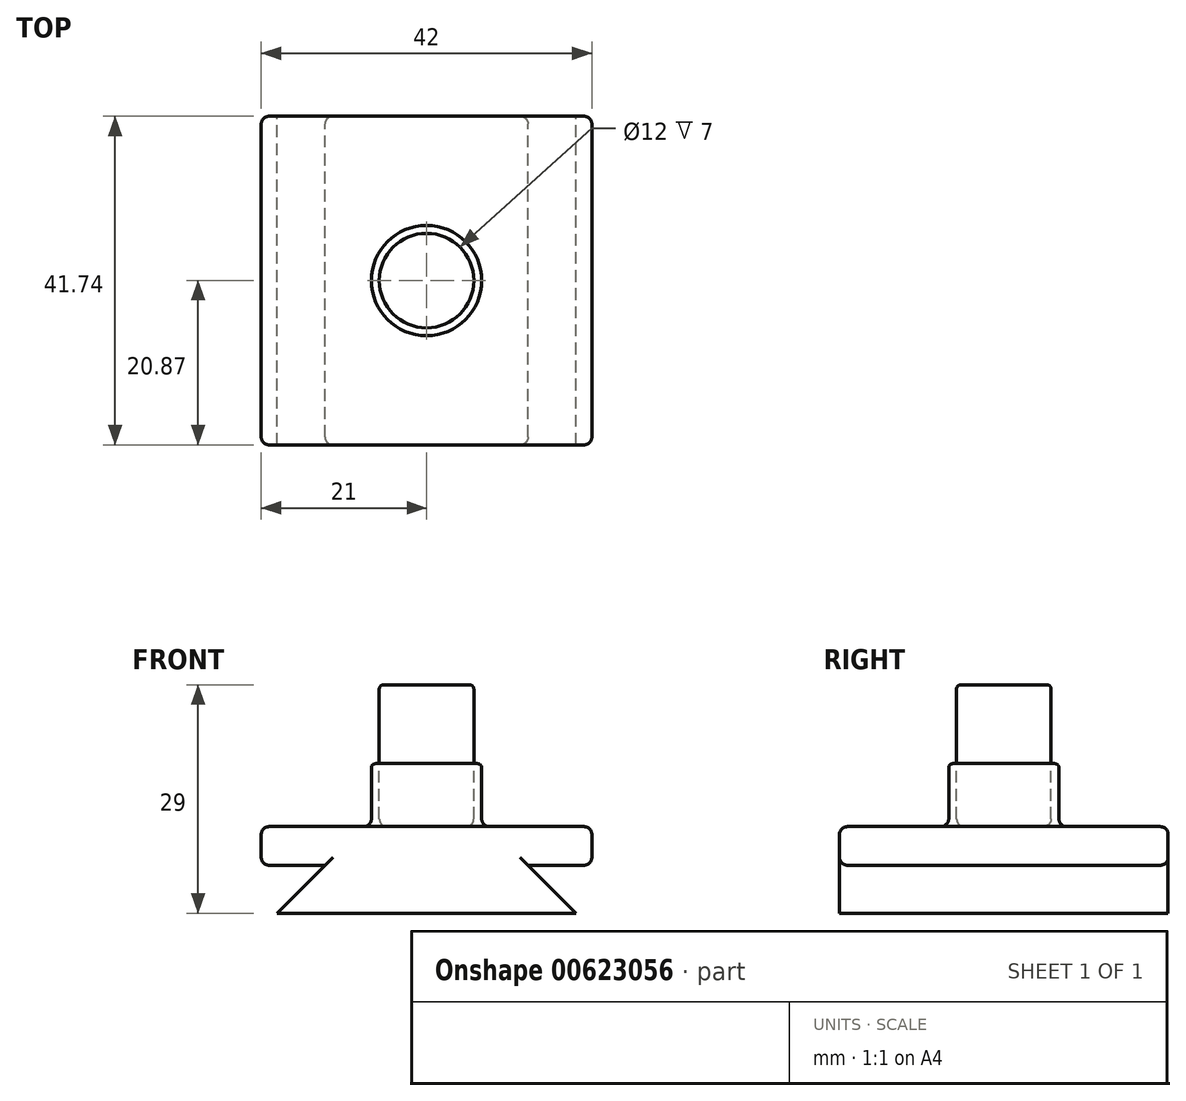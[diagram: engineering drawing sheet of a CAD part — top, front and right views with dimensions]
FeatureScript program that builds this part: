
annotation { "Feature Type Name" : "Feature", "Feature Type Description" : "" }
export const myFeature = defineFeature(function(context is Context, id is Id, definition is map)
    precondition{}
    {
        {
            var Q0;
            Q0=qCreatedBy(makeId("Front.planeOp"),FACE);
            var sketch = newSketch(context, id + "F0", { "sketchPlane" : qUnion([Q0])});
            skLineSegment(sketch, "E0", {"start": v(-19, 0) * mm, "end": v(0, 0) * mm});
            skLineSegment(sketch, "E1.bottom", {"start": v(-21, 11) * mm, "end": v(0, 11) * mm});
            skLineSegment(sketch, "E1.top", {"start": v(-21, 6.1) * mm, "end": v(0, 6.1) * mm});
            skLineSegment(sketch, "E1.left", {"start": v(-21, 11) * mm, "end": v(-21, 6.1) * mm});
            skLineSegment(sketch, "E1.right", {"start": v(0, 11) * mm, "end": v(0, 6.1) * mm});
            skLineSegment(sketch, "E2", {"start": v(-19, 0) * mm, "end": v(-12.9, 6.1) * mm});
            skLineSegment(sketch, "E3.top", {"start": v(0, 11) * mm, "end": v(-6, 11) * mm});
            skLineSegment(sketch, "E4.top", {"start": v(0, 11) * mm, "end": v(-7, 11) * mm});
            skLineSegment(sketch, "E5.MirrorCS", {"start": v(0, 11) * mm, "end": v(6, 11) * mm});
            skLineSegment(sketch, "E6.MirrorCS", {"start": v(0, 11) * mm, "end": v(7, 11) * mm});
            skLineSegment(sketch, "E7.MirrorCS", {"start": v(19, 0) * mm, "end": v(0, 0) * mm});
            skLineSegment(sketch, "E8.MirrorCS", {"start": v(19, 0) * mm, "end": v(12.9, 6.1) * mm});
            skLineSegment(sketch, "E9.MirrorCS", {"start": v(21, 11) * mm, "end": v(21, 6.1) * mm});
            skLineSegment(sketch, "E10.MirrorCS", {"start": v(21, 11) * mm, "end": v(0, 11) * mm});
            skLineSegment(sketch, "E11.MirrorCS", {"start": v(21, 6.1) * mm, "end": v(0, 6.1) * mm});
            skSolve(sketch);
        }
        {
            var Q0;
            {var subQ4=sQuery(id+"F0.wireOp",EDGE,"E1.bottom");Q0=makeQuery(id+"F0.imprint","IMPRINT",FACE,{"disambiguationData":[TD([[makeQuery(id+"F0.imprint","IMPRINT",EDGE,{"derivedFrom":subQ4}),-1.0]])]});}
            var Q1;
            {var subQ4=sQuery(id+"F0.wireOp",EDGE,"E1.right");Q1=makeQuery(id+"F0.imprint","IMPRINT",FACE,{"disambiguationData":[TD([[makeQuery(id+"F0.imprint","IMPRINT",EDGE,{"derivedFrom":subQ4}),1.0]])]});}
            var Q2;
            Q2=makeQuery(id+"F0.imprint","IMPRINT",FACE,{"disambiguationData":[TD([[makeQuery(id+"F0.imprint","IMPRINT",EDGE,{"derivedFrom":sQuery(id+"F0.wireOp",EDGE,"E0")}),1.0]])]});
            extrude(context, id + "F1", {"entities" : qUnion([Q0, Q1, Q2]), "endBound" : BoundingType.SYMMETRIC, "depth" : 41.74 * mm, "offsetDistance" : 25 * mm});
        }
        {
            var Q0;
            Q0=qCreatedBy(makeId("Front.planeOp"),FACE);
            var sketch = newSketch(context, id + "F2", { "sketchPlane" : qUnion([Q0])});
            skLineSegment(sketch, "E12.0", {"start": v(21, 11) * mm, "end": v(-21, 11) * mm});
            skLineSegment(sketch, "E12.1", {"start": v(-21, 11) * mm, "end": v(-21, 6.1) * mm});
            skLineSegment(sketch, "E12.2", {"start": v(-21, 6.1) * mm, "end": v(-12.9, 6.1) * mm});
            skLineSegment(sketch, "E12.3", {"start": v(-19, 0) * mm, "end": v(-12.9, 6.1) * mm});
            skLineSegment(sketch, "E12.4", {"start": v(19, 0) * mm, "end": v(12.9, 6.1) * mm});
            skLineSegment(sketch, "E12.5", {"start": v(21, 6.1) * mm, "end": v(12.9, 6.1) * mm});
            skLineSegment(sketch, "E12.6", {"start": v(21, 11) * mm, "end": v(21, 6.1) * mm});
            skLineSegment(sketch, "E12.7", {"start": v(-19, 0) * mm, "end": v(19, 0) * mm});
            skPoint(sketch, "E12.8", {"position": v(0, 11) * mm});
            skPoint(sketch, "E12.9", {"position": v(0, 0) * mm});
            skLineSegment(sketch, "E13.bottom", {"start": v(0, 29) * mm, "end": v(-6, 29) * mm});
            skLineSegment(sketch, "E13.top", {"start": v(0, 11) * mm, "end": v(-6, 11) * mm});
            skLineSegment(sketch, "E13.left", {"start": v(0, 29) * mm, "end": v(0, 11) * mm});
            skLineSegment(sketch, "E13.right", {"start": v(-6, 29) * mm, "end": v(-6, 11) * mm});
            skLineSegment(sketch, "E14.bottom", {"start": v(0, 19) * mm, "end": v(-7, 19) * mm});
            skLineSegment(sketch, "E14.top", {"start": v(0, 11) * mm, "end": v(-7, 11) * mm});
            skLineSegment(sketch, "E14.left", {"start": v(0, 19) * mm, "end": v(0, 11) * mm});
            skLineSegment(sketch, "E14.right", {"start": v(-7, 19) * mm, "end": v(-7, 11) * mm});
            skSolve(sketch);
        }
        {
            var Q0;
            {var subQ5=sQuery(id+"F2.wireOp",EDGE,"E14.left");Q0=makeQuery(id+"F2.imprint","IMPRINT",FACE,{"disambiguationData":[TD([[makeQuery(id+"F2.imprint","IMPRINT",EDGE,{"derivedFrom":subQ5}),-1.0]])]});}
            var Q1;
            {var subQ5=sQuery(id+"F2.wireOp",EDGE,"E14.right");Q1=makeQuery(id+"F2.imprint","IMPRINT",FACE,{"disambiguationData":[TD([[makeQuery(id+"F2.imprint","IMPRINT",EDGE,{"derivedFrom":subQ5}),1.0]])]});}
            var Q2;
            {var subQ0=sQuery(id+"F2.wireOp",EDGE,"E13.bottom");Q2=makeQuery(id+"F2.imprint","IMPRINT",FACE,{"disambiguationData":[TD([[makeQuery(id+"F2.imprint","IMPRINT",EDGE,{"derivedFrom":subQ0}),1.0]])]});}
            var Q3;
            Q3=sQuery(id+"F2.wireOp",EDGE,"E13.left");
            revolve(context, id + "F3", {"operationType" : NewBodyOperationType.ADD, "entities" : qUnion([Q0, Q1, Q2]), "axis" : qUnion([Q3]), "revolveType" : RevolveType.FULL});
        }
        {
            var Q0;
            Q0=makeQuery(id+"F3.opRevolve","SWEPT_EDGE",EDGE,{"disambiguationData":[OSD([sQuery(id+"F2.wireOp",EDGE,"E13.bottom"),sQuery(id+"F2.wireOp",EDGE,"E13.right")])]});
            var Q1;
            Q1=makeQuery(id+"F3.opRevolve","SWEPT_EDGE",EDGE,{"disambiguationData":[OSD([sQuery(id+"F2.wireOp",EDGE,"E14.bottom"),sQuery(id+"F2.wireOp",EDGE,"E14.right")])]});
            fillet(context, id + "F4", {"entities" : qUnion([Q0, Q1]), "radius" : 0.5 * mm, "tangentPropagation" : true, "allowEdgeOverflow" : false});
        }
        {
            var Q0;
            Q0=makeQuery(id+"F1.opExtrude","SWEPT_FACE",FACE,{"disambiguationData":[OSD([sQuery(id+"F0.wireOp",EDGE,"E1.bottom"),sQuery(id+"F0.wireOp",EDGE,"E4.top"),sQuery(id+"F0.wireOp",EDGE,"E10.MirrorCS")])]});
            var Q1;
            Q1=makeQuery(id+"F1.opExtrude","SWEPT_FACE",FACE,{"disambiguationData":[OSD([sQuery(id+"F0.wireOp",EDGE,"E1.left")])]});
            var Q2;
            Q2=makeQuery(id+"F1.opExtrude","SWEPT_FACE",FACE,{"disambiguationData":[OSD([sQuery(id+"F0.wireOp",EDGE,"E9.MirrorCS")])]});
            var Q3;
            Q3=makeQuery(id+"F1.opExtrude","CAP_EDGE",EDGE,{"disambiguationData":[OSD([sQuery(id+"F0.wireOp",EDGE,"E11.MirrorCS")])],"isStart":true});
            var Q4;
            Q4=makeQuery(id+"F1.opExtrude","CAP_EDGE",EDGE,{"disambiguationData":[OSD([sQuery(id+"F0.wireOp",EDGE,"E1.top")])],"isStart":true});
            var Q5;
            Q5=makeQuery(id+"F1.opExtrude","CAP_EDGE",EDGE,{"disambiguationData":[OSD([sQuery(id+"F0.wireOp",EDGE,"E1.top")])],"isStart":false});
            var Q6;
            Q6=makeQuery(id+"F1.opExtrude","CAP_EDGE",EDGE,{"disambiguationData":[OSD([sQuery(id+"F0.wireOp",EDGE,"E11.MirrorCS")])],"isStart":false});
            fillet(context, id + "F5", {"entities" : qUnion([Q0, Q1, Q2, Q3, Q4, Q5, Q6]), "radius" : 1 * mm, "tangentPropagation" : true, "allowEdgeOverflow" : false});
        }
    });
